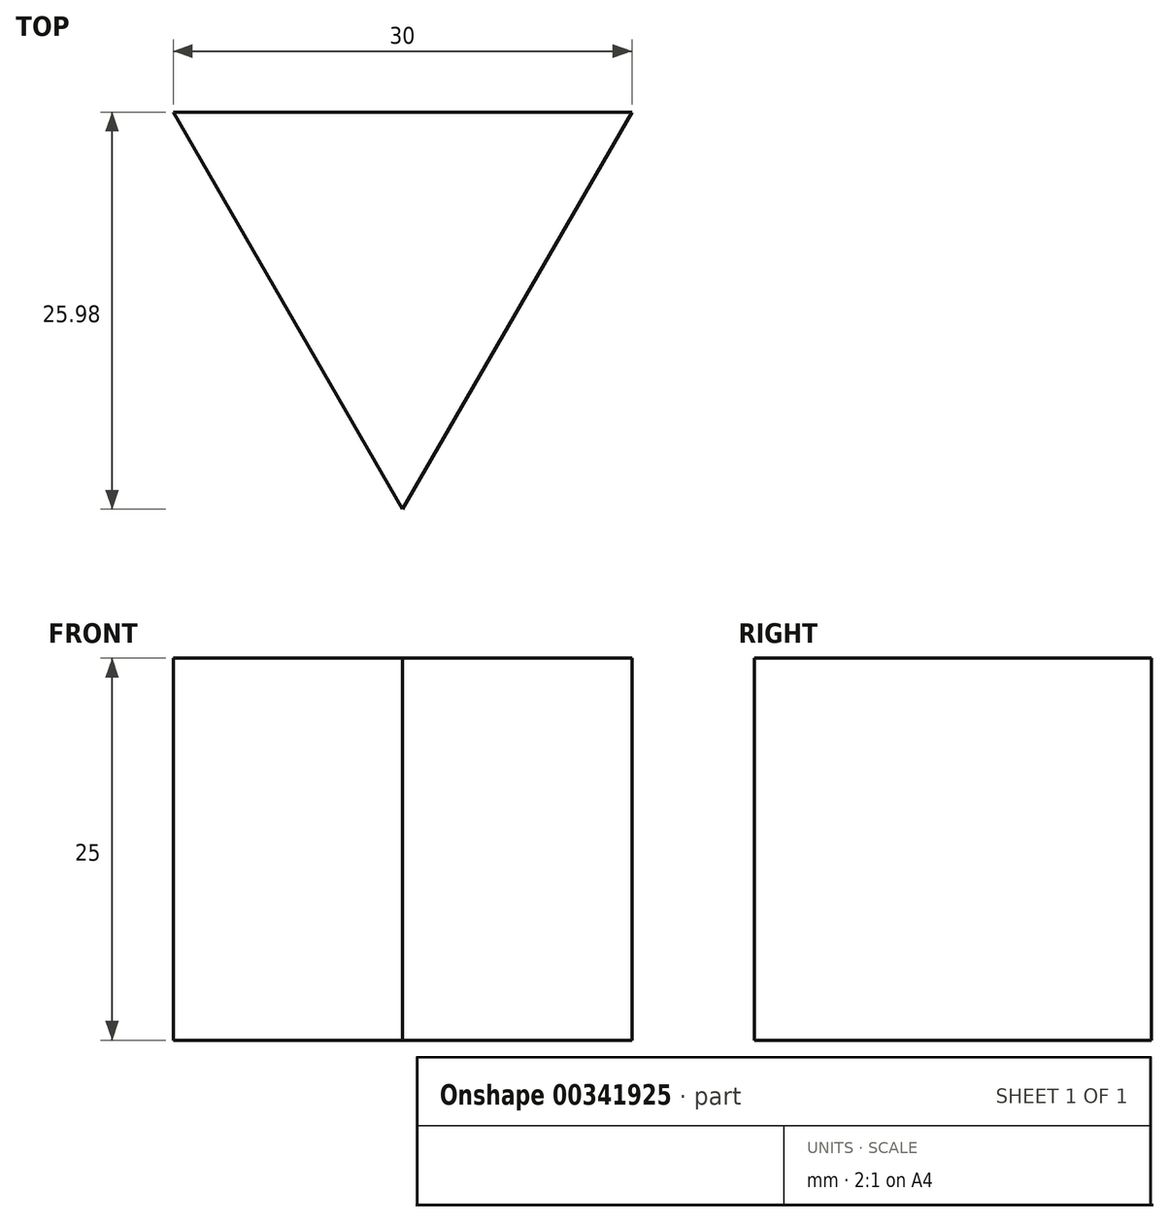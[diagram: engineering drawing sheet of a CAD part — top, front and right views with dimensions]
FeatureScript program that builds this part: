
annotation { "Feature Type Name" : "Feature", "Feature Type Description" : "" }
export const myFeature = defineFeature(function(context is Context, id is Id, definition is map)
    precondition{}
    {
        {
            var Q0;
            Q0=qCreatedBy(makeId("Top.planeOp"),FACE);
            var sketch = newSketch(context, id + "F0", { "sketchPlane" : qUnion([Q0])});
            skLineSegment(sketch, "E0", {"start": v(-15, 25.98) * mm, "end": v(0, 0) * mm});
            skLineSegment(sketch, "E1", {"start": v(0, 0) * mm, "end": v(15, 25.98) * mm});
            skLineSegment(sketch, "E2", {"start": v(-15, 25.98) * mm, "end": v(15, 25.98) * mm});
            skArc(sketch, "E3", {"start": v(-15, 25.98) * mm, "mid": v(-7.5, 33.48) * mm, "end": v(0, 25.98) * mm});
            skArc(sketch, "E4", {"start": v(0, 25.98) * mm, "mid": v(7.5, 33.48) * mm, "end": v(15, 25.98) * mm});
            skSolve(sketch);
        }
        {
            var Q0;
            {var subQ0=sQuery(id+"F0.wireOp",EDGE,"E0");Q0=makeQuery(id+"F0.imprint","IMPRINT",FACE,{"disambiguationData":[TD([[makeQuery(id+"F0.imprint","IMPRINT",EDGE,{"derivedFrom":subQ0}),1.0]])]});}
            var Q1;
            {var subQ0=sQuery(id+"F0.wireOp",EDGE,"E3");Q1=makeQuery(id+"F0.imprint","IMPRINT",FACE,{"disambiguationData":[TD([[makeQuery(id+"F0.imprint","IMPRINT",EDGE,{"derivedFrom":subQ0}),-1.0]])]});}
            var Q2;
            {var subQ0=sQuery(id+"F0.wireOp",EDGE,"E4");Q2=makeQuery(id+"F0.imprint","IMPRINT",FACE,{"disambiguationData":[TD([[makeQuery(id+"F0.imprint","IMPRINT",EDGE,{"derivedFrom":subQ0}),-1.0]])]});}
            extrude(context, id + "F1", {"entities" : qUnion([Q0, Q1, Q2]), "depth" : 25 * mm});
        }
    });
